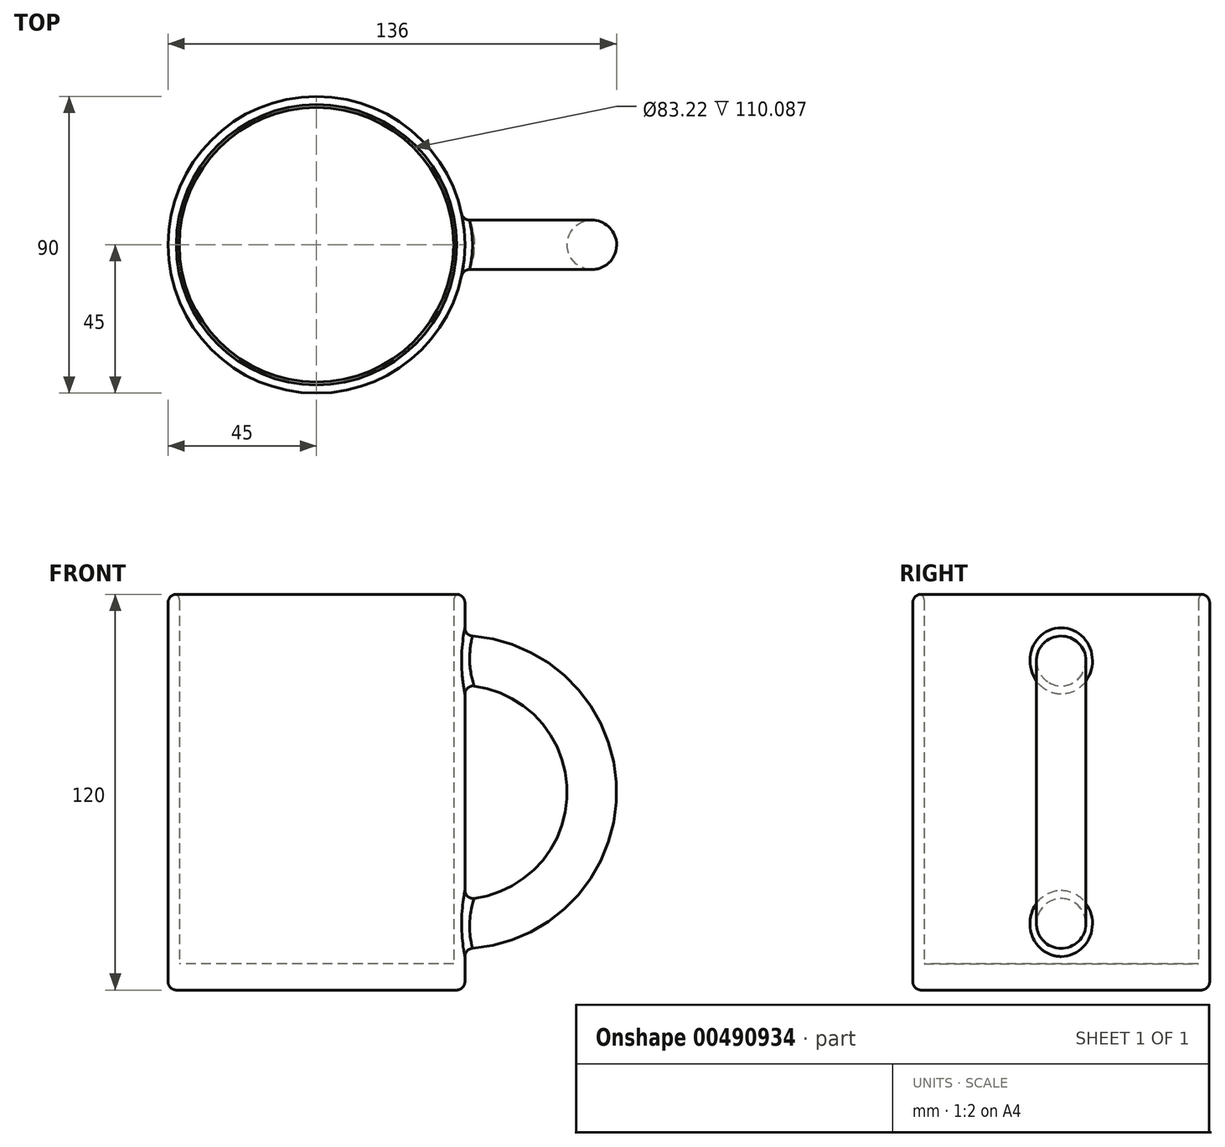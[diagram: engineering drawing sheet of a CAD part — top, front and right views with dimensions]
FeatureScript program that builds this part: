
annotation { "Feature Type Name" : "Feature", "Feature Type Description" : "" }
export const myFeature = defineFeature(function(context is Context, id is Id, definition is map)
    precondition{}
    {
        {
            var Q0;
            Q0=qCreatedBy(makeId("Top.planeOp"),FACE);
            var sketch = newSketch(context, id + "F0", { "sketchPlane" : qUnion([Q0])});
            skCircle(sketch, "E0", {"center": v(0, 0) * mm, "radius": 45 * mm});
            skCircle(sketch, "E1", {"center": v(0, 0) * mm, "radius": 41.6 * mm});
            skSolve(sketch);
        }
        {
            var Q0;
            Q0 = qSketchRegion(id + "F0", true);
            extrude(context, id + "F1", {"entities" : qUnion([Q0]), "depth" : 120 * mm});
        }
        {
            var Q0;
            Q0=qCreatedBy(makeId("Top.planeOp"),FACE);
            var sketch = newSketch(context, id + "F2", { "sketchPlane" : qUnion([Q0])});
            skCircle(sketch, "E2", {"center": v(0, 0) * mm, "radius": 44.5 * mm});
            skSolve(sketch);
        }
        {
            var Q0;
            Q0 = qSketchRegion(id + "F2", true);
            extrude(context, id + "F3", {"entities" : qUnion([Q0]), "operationType" : NewBodyOperationType.ADD, "depth" : 8 * mm});
        }
        {
            var Q0;
            Q0=qCreatedBy(makeId("Right.planeOp"),FACE);
            cPlane(context, id + "F4", {"entities" : qUnion([Q0]), "cplaneType" : CPlaneType.OFFSET, "offset" : 43.5 * mm, "width" : 150 * mm, "height" : 150 * mm});
        }
        {
            var Q0;
            Q0=qCreatedBy(id+"F4.planeOp",FACE);
            var sketch = newSketch(context, id + "F5", { "sketchPlane" : qUnion([Q0])});
            skCircle(sketch, "E3", {"center": v(0, 20) * mm, "radius": 7.5 * mm});
            skLineSegment(sketch, "E4", {"start": v(0, 60) * mm, "end": v(0, 20) * mm});
            skLineSegment(sketch, "E5", {"start": v(-82.67, 60) * mm, "end": v(87.73, 60) * mm});
            skSolve(sketch);
        }
        {
            var Q0;
            Q0 = qSketchRegion(id + "F5", true);
            var Q1;
            Q1=sQuery(id+"F5.wireOp",EDGE,"E5");
            revolve(context, id + "F6", {"operationType" : NewBodyOperationType.ADD, "entities" : qUnion([Q0]), "axis" : qUnion([Q1]), "revolveType" : RevolveType.ONE_DIRECTION, "oppositeDirection" : true, "angle" : 180 * degree});
        }
        {
            var Q0;
            Q0=makeQuery(id+"F1.opExtrude","CAP_EDGE",EDGE,{"disambiguationData":[OSD([sQuery(id+"F0.wireOp",EDGE,"E0")])],"isStart":false});
            fillet(context, id + "F7", {"entities" : qUnion([Q0]), "radius" : 2.5 * mm, "tangentPropagation" : true, "allowEdgeOverflow" : false});
        }
        {
            var Q0;
            Q0=makeQuery(id+"F1.opExtrude","CAP_EDGE",EDGE,{"disambiguationData":[OSD([sQuery(id+"F0.wireOp",EDGE,"E1")])],"isStart":false});
            fillet(context, id + "F8", {"entities" : qUnion([Q0]), "radius" : 2.5 * mm, "tangentPropagation" : true, "allowEdgeOverflow" : false});
        }
        {
            var Q0;
            Q0=makeQuery(id+"F1.opExtrude","CAP_EDGE",EDGE,{"disambiguationData":[OSD([sQuery(id+"F0.wireOp",EDGE,"E0")])],"isStart":true});
            fillet(context, id + "F9", {"entities" : qUnion([Q0]), "radius" : 2.5 * mm, "tangentPropagation" : true, "allowEdgeOverflow" : false});
        }
        {
            var Q0;
            Q0=makeQuery(id+"F6.opRevolve","SWEPT_FACE",FACE,{"disambiguationData":[OSD([sQuery(id+"F5.wireOp",EDGE,"E3")])]});
            fillet(context, id + "F10", {"entities" : qUnion([Q0]), "radius" : 2.5 * mm, "tangentPropagation" : true, "allowEdgeOverflow" : false});
        }
    });
